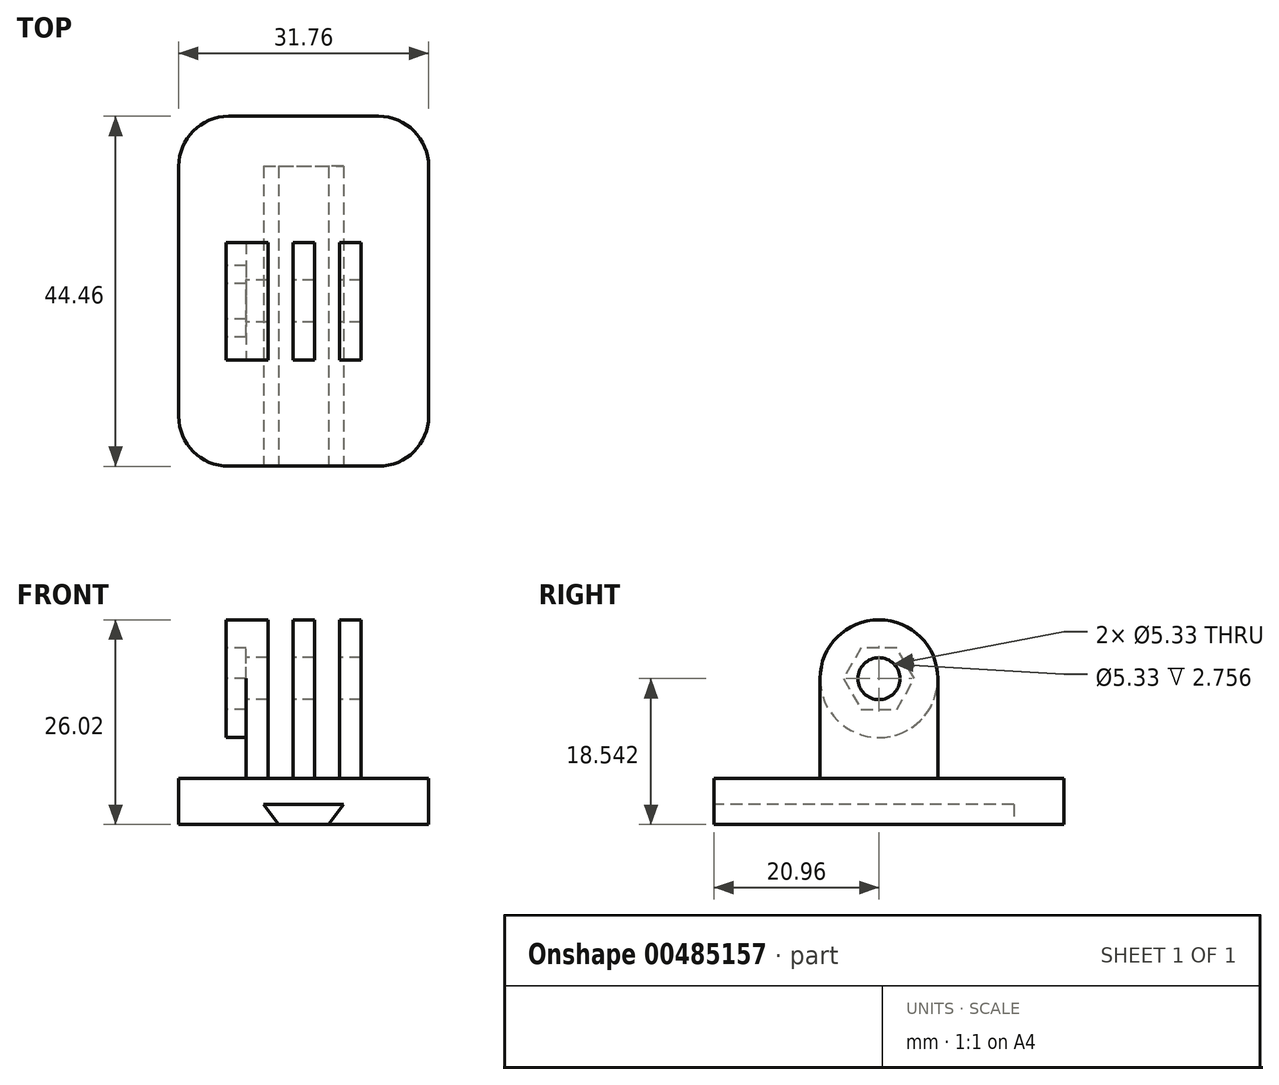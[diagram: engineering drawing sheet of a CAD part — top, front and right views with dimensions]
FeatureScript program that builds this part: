
annotation { "Feature Type Name" : "Feature", "Feature Type Description" : "" }
export const myFeature = defineFeature(function(context is Context, id is Id, definition is map)
    precondition{}
    {
        {
            var Q0;
            Q0=qCreatedBy(makeId("Top.planeOp"),FACE);
            var sketch = newSketch(context, id + "F0", { "sketchPlane" : qUnion([Q0])});
            skLineSegment(sketch, "E0.bottom", {"start": v(-15.88, 22.23) * mm, "end": v(15.88, 22.23) * mm});
            skLineSegment(sketch, "E0.top", {"start": v(-15.88, -22.23) * mm, "end": v(15.88, -22.23) * mm});
            skLineSegment(sketch, "E0.left", {"start": v(-15.88, 22.23) * mm, "end": v(-15.88, -22.22) * mm});
            skLineSegment(sketch, "E0.right", {"start": v(15.88, 22.23) * mm, "end": v(15.88, -22.22) * mm});
            skSolve(sketch);
        }
        {
            var Q0;
            Q0=makeQuery(id+"F0.imprint","IMPRINT",FACE,{"disambiguationData":[TD([[makeQuery(id+"F0.imprint","IMPRINT",EDGE,{"derivedFrom":sQuery(id+"F0.wireOp",EDGE,"E0.bottom")}),-1.0]])]});
            extrude(context, id + "F1", {"entities" : qUnion([Q0]), "depth" : 5.84 * mm});
        }
        {
            var Q0;
            Q0=makeQuery(id+"F1.opExtrude","SWEPT_FACE",FACE,{"disambiguationData":[OSD([sQuery(id+"F0.wireOp",EDGE,"E0.top")])]});
            var sketch = newSketch(context, id + "F2", { "sketchPlane" : qUnion([Q0])});
            skPoint(sketch, "E1.endSnap0", {"position": v(0, 0) * mm});
            skLineSegment(sketch, "E2", {"start": v(0, 2.54) * mm, "end": v(5.08, 2.54) * mm});
            skLineSegment(sketch, "E3", {"start": v(5.08, 2.54) * mm, "end": v(3.18, 0) * mm});
            skLineSegment(sketch, "E4", {"start": v(0, 2.54) * mm, "end": v(-5.08, 2.54) * mm});
            skLineSegment(sketch, "E5", {"start": v(-5.08, 2.54) * mm, "end": v(-3.18, 0) * mm});
            skSolve(sketch);
        }
        {
            var Q0;
            Q0=makeQuery(id+"F2.imprint","IMPRINT",FACE,{"disambiguationData":[TD([[makeQuery(id+"F2.imprint","IMPRINT",EDGE,{"derivedFrom":sQuery(id+"F2.wireOp",EDGE,"E2")}),-1.0]])]});
            extrude(context, id + "F3", {"entities" : qUnion([Q0]), "operationType" : NewBodyOperationType.REMOVE, "oppositeDirection" : true, "depth" : 38.1 * mm});
        }
        {
            var Q0;
            Q0=qCreatedBy(makeId("Right.planeOp"),FACE);
            var sketch = newSketch(context, id + "F4", { "sketchPlane" : qUnion([Q0])});
            skLineSegment(sketch, "E6.bottom", {"start": v(-8.75, 5.84) * mm, "end": v(6.21, 5.84) * mm});
            skLineSegment(sketch, "E6.left", {"start": v(-8.75, 5.84) * mm, "end": v(-8.75, 18.54) * mm});
            skLineSegment(sketch, "E6.right", {"start": v(6.21, 5.84) * mm, "end": v(6.21, 18.54) * mm});
            skCircle(sketch, "E7", {"center": v(-1.27, 18.54) * mm, "radius": 2.67 * mm});
            skArc(sketch, "E8", {"start": v(-8.75, 18.54) * mm, "mid": v(-1.27, 26.02) * mm, "end": v(6.21, 18.54) * mm});
            skSolve(sketch);
        }
        {
            var Q0;
            Q0=makeQuery(id+"F4.imprint","IMPRINT",FACE,{"disambiguationData":[TD([[makeQuery(id+"F4.imprint","IMPRINT",EDGE,{"derivedFrom":sQuery(id+"F4.wireOp",EDGE,"E6.bottom")}),1.0]])]});
            extrude(context, id + "F5", {"entities" : qUnion([Q0]), "operationType" : NewBodyOperationType.ADD, "endBound" : BoundingType.SYMMETRIC, "depth" : 19.68 * mm});
        }
        {
            var Q0;
            Q0=makeQuery(id+"F5.opExtrude","SWEPT_FACE",FACE,{"disambiguationData":[OSD([sQuery(id+"F4.wireOp",EDGE,"E6.left")])]});
            var sketch = newSketch(context, id + "F6", { "sketchPlane" : qUnion([Q0])});
            skLineSegment(sketch, "E9", {"start": v(-7.3, 5.84) * mm, "end": v(-7.3, 11.06) * mm});
            skLineSegment(sketch, "E10", {"start": v(-7.3, 11.06) * mm, "end": v(-9.84, 11.06) * mm});
            skLineSegment(sketch, "E11", {"start": v(7.3, 5.84) * mm, "end": v(7.3, 26.02) * mm});
            skLineSegment(sketch, "E12", {"start": v(-9.84, 11.06) * mm, "end": v(-9.84, 5.84) * mm});
            skLineSegment(sketch, "E13", {"start": v(-9.84, 5.84) * mm, "end": v(-7.3, 5.84) * mm});
            skLineSegment(sketch, "E14", {"start": v(7.3, 5.84) * mm, "end": v(9.84, 5.84) * mm});
            skLineSegment(sketch, "E15", {"start": v(1.37, 5.84) * mm, "end": v(4.55, 5.84) * mm});
            skLineSegment(sketch, "E16", {"start": v(4.55, 5.84) * mm, "end": v(4.55, 26.02) * mm});
            skLineSegment(sketch, "E17", {"start": v(4.55, 26.02) * mm, "end": v(1.37, 26.02) * mm});
            skLineSegment(sketch, "E18", {"start": v(1.37, 26.02) * mm, "end": v(1.37, 5.84) * mm});
            skLineSegment(sketch, "E19.bottom", {"start": v(-4.55, 5.84) * mm, "end": v(-1.37, 5.84) * mm});
            skLineSegment(sketch, "E19.top", {"start": v(-4.55, 26.02) * mm, "end": v(-1.37, 26.02) * mm});
            skLineSegment(sketch, "E19.left", {"start": v(-4.55, 5.84) * mm, "end": v(-4.55, 26.02) * mm});
            skLineSegment(sketch, "E19.right", {"start": v(-1.37, 5.84) * mm, "end": v(-1.37, 26.02) * mm});
            skLineSegment(sketch, "E20", {"start": v(9.84, 5.84) * mm, "end": v(9.84, 26.02) * mm});
            skLineSegment(sketch, "E21", {"start": v(9.84, 26.02) * mm, "end": v(7.3, 26.02) * mm});
            skSolve(sketch);
        }
        {
            var Q0;
            {var subQ0=sQuery(id+"F6.wireOp",EDGE,"E21");Q0=makeQuery(id+"F6.imprint","IMPRINT",FACE,{"disambiguationData":[TD([[makeQuery(id+"F6.imprint","IMPRINT",EDGE,{"derivedFrom":subQ0}),1.0]])]});}
            var Q1;
            {var subQ0=sQuery(id+"F6.wireOp",EDGE,"E14");Q1=makeQuery(id+"F6.imprint","IMPRINT",FACE,{"disambiguationData":[TD([[makeQuery(id+"F6.imprint","IMPRINT",EDGE,{"derivedFrom":subQ0}),-1.0]])]});}
            var Q2;
            {var subQ0=sQuery(id+"F6.wireOp",EDGE,"E17");Q2=makeQuery(id+"F6.imprint","IMPRINT",FACE,{"disambiguationData":[TD([[makeQuery(id+"F6.imprint","IMPRINT",EDGE,{"derivedFrom":subQ0}),1.0]])]});}
            var Q3;
            {var subQ0=sQuery(id+"F6.wireOp",EDGE,"E15");Q3=makeQuery(id+"F6.imprint","IMPRINT",FACE,{"disambiguationData":[TD([[makeQuery(id+"F6.imprint","IMPRINT",EDGE,{"derivedFrom":subQ0}),-1.0]])]});}
            var Q4;
            {var subQ0=sQuery(id+"F6.wireOp",EDGE,"E19.top");Q4=makeQuery(id+"F6.imprint","IMPRINT",FACE,{"disambiguationData":[TD([[makeQuery(id+"F6.imprint","IMPRINT",EDGE,{"derivedFrom":subQ0}),-1.0]])]});}
            var Q5;
            {var subQ0=sQuery(id+"F6.wireOp",EDGE,"E19.bottom");Q5=makeQuery(id+"F6.imprint","IMPRINT",FACE,{"disambiguationData":[TD([[makeQuery(id+"F6.imprint","IMPRINT",EDGE,{"derivedFrom":subQ0}),-1.0]])]});}
            var Q6;
            Q6=makeQuery(id+"F6.imprint","IMPRINT",FACE,{"disambiguationData":[TD([[makeQuery(id+"F6.imprint","IMPRINT",EDGE,{"derivedFrom":sQuery(id+"F6.wireOp",EDGE,"E9")}),1.0]])]});
            extrude(context, id + "F7", {"entities" : qUnion([Q0, Q1, Q2, Q3, Q4, Q5, Q6]), "operationType" : NewBodyOperationType.REMOVE, "oppositeDirection" : true, "depth" : 25.4 * mm});
        }
        {
            var Q0;
            Q0=makeQuery(id+"F5.opExtrude","CAP_FACE",FACE,{"disambiguationData":[OSD([sQuery(id+"F4.wireOp",EDGE,"E6.bottom"),sQuery(id+"F4.wireOp",EDGE,"E6.left"),sQuery(id+"F4.wireOp",EDGE,"E6.right"),sQuery(id+"F4.wireOp",EDGE,"E7"),sQuery(id+"F4.wireOp",EDGE,"E8")])],"isStart":true});
            var sketch = newSketch(context, id + "F8", { "sketchPlane" : qUnion([Q0])});
            skArc(sketch, "E22", {"start": v(-6.21, 18.54) * mm, "mid": v(1.27, 11.06) * mm, "end": v(8.75, 18.54) * mm});
            skLineSegment(sketch, "E23", {"start": v(8.75, 18.54) * mm, "end": v(8.75, 11.06) * mm});
            skLineSegment(sketch, "E24", {"start": v(8.75, 11.06) * mm, "end": v(-6.21, 11.06) * mm});
            skLineSegment(sketch, "E25", {"start": v(-6.21, 11.06) * mm, "end": v(-6.21, 18.54) * mm});
            skSolve(sketch);
        }
        {
            var Q0;
            {var subQ0=sQuery(id+"F8.wireOp",EDGE,"E25");Q0=makeQuery(id+"F8.imprint","IMPRINT",FACE,{"disambiguationData":[TD([[makeQuery(id+"F8.imprint","IMPRINT",EDGE,{"derivedFrom":subQ0}),-1.0]])]});}
            var Q1;
            {var subQ0=sQuery(id+"F8.wireOp",EDGE,"E23");Q1=makeQuery(id+"F8.imprint","IMPRINT",FACE,{"disambiguationData":[TD([[makeQuery(id+"F8.imprint","IMPRINT",EDGE,{"derivedFrom":subQ0}),1.0]])]});}
            extrude(context, id + "F9", {"entities" : qUnion([Q0, Q1]), "operationType" : NewBodyOperationType.REMOVE, "oppositeDirection" : true, "depth" : 2.54 * mm});
        }
        {
            var Q0;
            Q0=makeQuery(id+"F1.opExtrude","SWEPT_EDGE",EDGE,{"disambiguationData":[OSD([sQuery(id+"F0.wireOp",EDGE,"E0.bottom"),sQuery(id+"F0.wireOp",EDGE,"E0.right")])]});
            var Q1;
            Q1=makeQuery(id+"F1.opExtrude","SWEPT_EDGE",EDGE,{"disambiguationData":[OSD([sQuery(id+"F0.wireOp",EDGE,"E0.bottom"),sQuery(id+"F0.wireOp",EDGE,"E0.left")])]});
            var Q2;
            Q2=makeQuery(id+"F1.opExtrude","SWEPT_EDGE",EDGE,{"disambiguationData":[OSD([sQuery(id+"F0.wireOp",EDGE,"E0.top"),sQuery(id+"F0.wireOp",EDGE,"E0.left")])]});
            var Q3;
            Q3=makeQuery(id+"F1.opExtrude","SWEPT_EDGE",EDGE,{"disambiguationData":[OSD([sQuery(id+"F0.wireOp",EDGE,"E0.top"),sQuery(id+"F0.wireOp",EDGE,"E0.right")])]});
            fillet(context, id + "F10", {"entities" : qUnion([Q0, Q1, Q2, Q3]), "radius" : 6.35 * mm, "tangentPropagation" : true, "allowEdgeOverflow" : false});
        }
        {
            var Q0;
            Q0=makeQuery(id+"F5.opExtrude","CAP_FACE",FACE,{"disambiguationData":[OSD([sQuery(id+"F4.wireOp",EDGE,"E6.bottom"),sQuery(id+"F4.wireOp",EDGE,"E6.left"),sQuery(id+"F4.wireOp",EDGE,"E6.right"),sQuery(id+"F4.wireOp",EDGE,"E7"),sQuery(id+"F4.wireOp",EDGE,"E8")])],"isStart":true});
            var sketch = newSketch(context, id + "F11", { "sketchPlane" : qUnion([Q0])});
            skCircle(sketch, "E26.cCircle", {"center": v(1.27, 18.54) * mm, "radius": 3.91 * mm, "construction": true});
            skLineSegment(sketch, "E26.0", {"start": v(-0.99, 22.45) * mm, "end": v(3.53, 22.45) * mm});
            skLineSegment(sketch, "E26.1", {"start": v(3.53, 22.45) * mm, "end": v(5.79, 18.54) * mm});
            skLineSegment(sketch, "E26.2", {"start": v(5.79, 18.54) * mm, "end": v(3.53, 14.63) * mm});
            skLineSegment(sketch, "E26.3", {"start": v(3.53, 14.63) * mm, "end": v(-0.99, 14.63) * mm});
            skLineSegment(sketch, "E26.4", {"start": v(-0.99, 14.63) * mm, "end": v(-3.25, 18.54) * mm});
            skLineSegment(sketch, "E26.5", {"start": v(-3.25, 18.54) * mm, "end": v(-0.99, 22.45) * mm});
            skPoint(sketch, "E26.0.midPoint", {"position": v(1.27, 22.45) * mm});
            skSolve(sketch);
        }
        {
            var Q0;
            Q0=makeQuery(id+"F11.imprint","IMPRINT",FACE,{"disambiguationData":[TD([[makeQuery(id+"F11.imprint","IMPRINT",EDGE,{"derivedFrom":sQuery(id+"F11.wireOp",EDGE,"E26.0")}),-1.0]])]});
            extrude(context, id + "F12", {"entities" : qUnion([Q0]), "operationType" : NewBodyOperationType.REMOVE, "oppositeDirection" : true, "depth" : 2.54 * mm});
        }
    });
